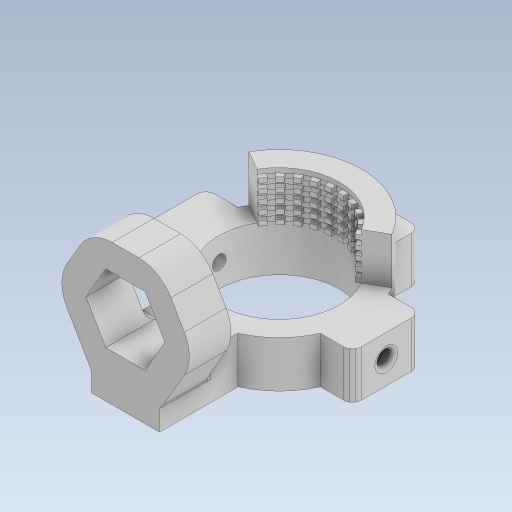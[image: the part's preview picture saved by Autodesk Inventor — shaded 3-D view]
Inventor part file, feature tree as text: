
AUTODESK INVENTOR PART (.ipt)
format: ipt  version: 2023 (Build 270158000, 158)  size: 1,103,872 bytes
history: native  units: in
note: dims shown in document units (in); Inventor stores cm internally (conversion verified against a paired STEP export)
features: sketch x7, extrude x5, fillet x3, projected_geometry x3, revolve x1, hole x1
ambient origin geometry x8: Origin, YZ Plane, XZ Plane, XY Plane, X Axis, Y Axis, Z Axis, Center Point
bodies: Solid1 (feature_tree)
feature tree (20):
  extrude  "Extrusion1"  Depth=0.3937in TaperAngle=0.0deg
  extrude  "Extrusion2"  Depth=0.3937in TaperAngle=0.0deg
  extrude  "Extrusion3"  Depth=0.0394in TaperAngle=120.0deg
  revolve  "Revolution1"  [1 undecoded]
  extrude  "Extrusion16"  Depth=0.3937in TaperAngle=0.0deg
  extrude  "Extrusion18"  Depth=0.5906in
  fillet  "Fillet6"  Radius=0.3543in
  fillet  "Fillet7"  Radius=0.315in
  hole  "Hole4"  [1 undecoded]
  fillet  "Fillet8"  Radius=0.0344in
  sketch  "Sketch1"  dims[d0=1.0236in d1=0.3937in d2=0.0in]
  sketch  "Sketch2"  dims[d3=120.0deg d4=0.3937in d5=0.0in]
  sketch  "Sketch3"  dims[d6=0.0394in d7=7.874in d9=120.0deg]
  sketch  "Sketch4"  dims[d11=0.3937in d12=0.0in d14=3.937in d16=0.0394in d17=0.3937in d19=0.3937in]
  sketch  "Sketch29"  dims[d21=360.0deg d122=0.3937in d123=0.1969in d124=0.0in d125=0.0in]
  projected_geometry  "Projected Loop12"
  projected_geometry  "Projected Loop13"
  projected_geometry  "Projected Loop14"
  sketch  "Sketch32"  dims[d132=0.3346in d133=0.5906in d134=0.3543in d135=0.0in d136=0.315in]
  sketch  "Sketch33"  dims[d137=0.0787in d138=0.1181in d139=0.2362in d140=0.507in d141=0.0787in d142=0.5635in d143=0.315in d144=0.8108in d145=0.0394in d91=0.0344in d92=0.0344in d93=0.0197in d94=0.0344in]
note: 2 required parameter values undecoded (feature->parameter linkage not recoverable at this tier; creation-order binding heuristic only, values carry confidence <= 0.55)